# Revit family: Edge_TB42_I_Top_Hung_Standard
name_source: partatom
category: Windows
revit_build: Autodesk Revit 2014 (Build: 20130308_1515(x64)
units: mm (PartAtom-declared; Revit-internal decimal feet)

## types (24) — shared parameters
Aluminium Thickness = 1 mm  [stored 0.00328084 ft]
Bead SG Gap = 13 mm
Bottom Hung = No
Casement Dimension = 42 mm  [stored 0.137795 ft]
Custom Sash Bottom Height = 554 mm  [stored 1.81759 ft]
Custom Sash Top Height = 554 mm  [stored 1.81759 ft]
DG Extrusion Start = 11 mm  [stored 0.0360892 ft]
DG Gasket Finish = Double Glazing Gasket Material
Default Sill Height = 800 mm  [stored 2.62467 ft]
Depth Bead = 28 mm  [stored 0.0918635 ft]
Depth Mullion = 1 mm  [stored 0.00328084 ft]
Description = Thermal break casement windows (42mm), Type I top hung
Frame Center Offset = 21 mm  [stored 0.0688976 ft]
Has Stiffener Cap = Yes
Height Panel 1 = 540 mm  [stored 1.77165 ft]
Height Panel 2 = 540 mm  [stored 1.77165 ft]
Height Sash Bottom = 524 mm  [stored 1.71916 ft]
Height Sash Bottom Opening = 554 mm  [stored 1.81759 ft]
Height Sash Top = 524 mm  [stored 1.71916 ft]
Height Sash Top Opening = 554 mm  [stored 1.81759 ft]
Limit Fixed Pane Height Max = 1800 mm
Limit Fixed Pane Height Min = 200 mm  [stored 0.656168 ft]
Limit Fixed Pane Width Max = 1500 mm
Limit Fixed Pane Width Min = 200 mm  [stored 0.656168 ft]
Limit Sash Bottom Height Min = 300 mm  [stored 0.984252 ft]
Limit Sash Top Height Max = 1200 mm
Limit Sash Top Height Min = 300 mm  [stored 0.984252 ft]
Limit Sash Width Max = 1500 mm
Limit Sash Width Min = 300 mm  [stored 0.984252 ft]
Limit Window Height Max = 1860 mm
Limit Window Height Min = 1400 mm
Manufacturer = Crealco
Max System DG One Piece Thickness = 6 mm  [stored 0.019685 ft]
Max System DG Unit Thickness = 25 mm  [stored 0.082021 ft]
Model = Edge
Mullion Depth Windload Based = 1 mm  [stored 0.00328084 ft]
Offset Bead SG Center Reversed = 21 mm  [stored 0.0688976 ft]
Offset Panel 3 Bead Top = 1170 mm
Offset Sash 1 Top = 23 mm  [stored 0.0754593 ft]
Offset Sash 2 Top = 593 mm  [stored 1.94554 ft]
Offset Sash Left = 23 mm  [stored 0.0754593 ft]
Offset Transom 1 Top = 570 mm  [stored 1.87008 ft]
Offset Transom 2 Top = 1140 mm
Offset Window Exterior = 21 mm  [stored 0.0688976 ft]
SG Gasket Thickness = 6 mm  [stored 0.019685 ft]
Sash Center Offset = 18 mm
Sash Overlap = 7 mm  [stored 0.0229659 ft]
Sash Spacing Inner = 8 mm  [stored 0.0262467 ft]
Top Hung = Yes
URL = http://www.crealco.co.za
Wall Closure = By host
Width Bead = 15 mm  [stored 0.0492126 ft]
Width Profile = 30 mm  [stored 0.0984252 ft]
zero-valued in all types: Window Exterior Offset

## per-type parameters (varying)
- EDGE-1215DT-1000Pa: Area Pane Left Bottom=0.15 m²; Area Pane Left Middle=0.23 m²; Area Pane Left Top=0.23 m²; Area Pane Right=0.78 m²; Clearvue Insulated LowE SHGC Value=0.727; Clearvue Insulated LowE U Value=3.36; Clearvue Insulated SHGC Value=0.8; Clearvue Insulated U Value=4.09; Clearvue SHGC Value=0.888; Clearvue U Value=7.3; Custom Sash Width=554 mm  [stored 1.81759 ft]; Custom Windload=1000 mm  [stored 3.28084 ft]; Custom Window Height=1490 mm; Custom Window Width=1190 mm; DG Thickness Calc=4 mm  [stored 0.0131234 ft]; Energy Advantage SHGC Value=0.794; Energy Advantage U Value=5.3; Height=1490 mm; Height Panel 3=290 mm  [stored 0.951444 ft]; Height Panel 4=1430 mm; Intruderprufe Insulated LowE SHGC Value=0.664; Intruderprufe Insulated LowE U Value=3.31; Intruderprufe Insulated SHGC Value=0.734; Intruderprufe Insulated U Value=4.03; Intruderprufe LowE SHGC Value=0.74; Intruderprufe LowE U Value=5.28; Intruderprufe SHGC Value=0.829; Intruderprufe U Value=7.17; Length Mullion=1490 mm; Length Transom=540 mm  [stored 1.77165 ft]; Limit Sash Bottom Height Max=644 mm  [stored 2.11286 ft]; Limit Sash Bottom Height Max Based On Top Sash=644 mm  [stored 2.11286 ft]; Limit Sash Bottom Height Max Calc=644 mm  [stored 2.11286 ft]; Limit Window Width Max=2130 mm; Limit Window Width Min=830 mm  [stored 2.7231 ft]; Max Pane Area=0.78 m²; Offset Mullion Left=570 mm  [stored 1.87008 ft]; Offset Panel 4 Left=600 mm  [stored 1.9685 ft]; Width=1190 mm; Width Panel 1=540 mm  [stored 1.77165 ft]; Width Panel 2=540 mm  [stored 1.77165 ft]; Width Panel 3=540 mm  [stored 1.77165 ft]; Width Panel 4=560 mm  [stored 1.83727 ft]; Width Sash 1=524 mm  [stored 1.71916 ft]; Width Sash 2=524 mm  [stored 1.71916 ft]; Width Sash Opening=554 mm  [stored 1.81759 ft]; Windload Design=1000 mm  [stored 3.28084 ft]
- EDGE-1515DT-1000Pa: Area Pane Left Bottom=0.15 m²; Area Pane Left Middle=0.23 m²; Area Pane Left Top=0.23 m²; Area Pane Right=1.21 m²; Clearvue Insulated LowE SHGC Value=0.839; Clearvue Insulated LowE U Value=3.59; Clearvue Insulated SHGC Value=0.923; Clearvue Insulated U Value=4.46; Clearvue SHGC Value=1.028; Clearvue U Value=8.22; Custom Sash Width=554 mm  [stored 1.81759 ft]; Custom Windload=1000 mm  [stored 3.28084 ft]; Custom Window Height=1490 mm; Custom Window Width=1490 mm; DG Thickness Calc=4 mm  [stored 0.0131234 ft]; Energy Advantage SHGC Value=0.919; Energy Advantage U Value=5.83; Height=1490 mm; Height Panel 3=290 mm  [stored 0.951444 ft]; Height Panel 4=1430 mm; Intruderprufe Insulated LowE SHGC Value=0.766; Intruderprufe Insulated LowE U Value=3.53; Intruderprufe Insulated SHGC Value=0.848; Intruderprufe Insulated U Value=4.39; Intruderprufe LowE SHGC Value=0.856; Intruderprufe LowE U Value=5.79; Intruderprufe SHGC Value=0.961; Intruderprufe U Value=8.07; Length Mullion=1490 mm; Length Transom=540 mm  [stored 1.77165 ft]; Limit Sash Bottom Height Max=644 mm  [stored 2.11286 ft]; Limit Sash Bottom Height Max Based On Top Sash=644 mm  [stored 2.11286 ft]; Limit Sash Bottom Height Max Calc=644 mm  [stored 2.11286 ft]; Limit Window Width Max=2130 mm; Limit Window Width Min=830 mm  [stored 2.7231 ft]; Max Pane Area=1.21 m²; Offset Mullion Left=570 mm  [stored 1.87008 ft]; Offset Panel 4 Left=600 mm  [stored 1.9685 ft]; Width=1490 mm; Width Panel 1=540 mm  [stored 1.77165 ft]; Width Panel 2=540 mm  [stored 1.77165 ft]; Width Panel 3=540 mm  [stored 1.77165 ft]; Width Panel 4=860 mm  [stored 2.82152 ft]; Width Sash 1=524 mm  [stored 1.71916 ft]; Width Sash 2=524 mm  [stored 1.71916 ft]; Width Sash Opening=554 mm  [stored 1.81759 ft]; Windload Design=1000 mm  [stored 3.28084 ft]
- EDGE-1218DT-1000Pa: Area Pane Left Bottom=0.31 m²; Area Pane Left Middle=0.23 m²; Area Pane Left Top=0.23 m²; Area Pane Right=0.95 m²; Clearvue Insulated LowE SHGC Value=0.789; Clearvue Insulated LowE U Value=3.47; Clearvue Insulated SHGC Value=0.868; Clearvue Insulated U Value=4.26; Clearvue SHGC Value=0.965; Clearvue U Value=7.76; Custom Sash Width=554 mm  [stored 1.81759 ft]; Custom Windload=1000 mm  [stored 3.28084 ft]; Custom Window Height=1790 mm; Custom Window Width=1190 mm; DG Thickness Calc=4 mm  [stored 0.0131234 ft]; Energy Advantage SHGC Value=0.863; Energy Advantage U Value=5.56; Height=1790 mm; Height Panel 3=590 mm; Height Panel 4=1730 mm; Intruderprufe Insulated LowE SHGC Value=0.721; Intruderprufe Insulated LowE U Value=3.41; Intruderprufe Insulated SHGC Value=0.797; Intruderprufe Insulated U Value=4.2; Intruderprufe LowE SHGC Value=0.804; Intruderprufe LowE U Value=5.53; Intruderprufe SHGC Value=0.902; Intruderprufe U Value=7.61; Length Mullion=1790 mm; Length Transom=540 mm  [stored 1.77165 ft]; Limit Sash Bottom Height Max=944 mm; Limit Sash Bottom Height Max Based On Top Sash=944 mm; Limit Sash Bottom Height Max Calc=944 mm; Limit Window Width Max=2130 mm; Limit Window Width Min=830 mm  [stored 2.7231 ft]; Max Pane Area=0.95 m²; Offset Mullion Left=570 mm  [stored 1.87008 ft]; Offset Panel 4 Left=600 mm  [stored 1.9685 ft]; Width=1190 mm; Width Panel 1=540 mm  [stored 1.77165 ft]; Width Panel 2=540 mm  [stored 1.77165 ft]; Width Panel 3=540 mm  [stored 1.77165 ft]; Width Panel 4=560 mm  [stored 1.83727 ft]; Width Sash 1=524 mm  [stored 1.71916 ft]; Width Sash 2=524 mm  [stored 1.71916 ft]; Width Sash Opening=554 mm  [stored 1.81759 ft]; Windload Design=1000 mm  [stored 3.28084 ft]
- EDGE-1518DT-1000Pa: Area Pane Left Bottom=0.31 m²; Area Pane Left Middle=0.23 m²; Area Pane Left Top=0.23 m²; Area Pane Right=1.46 m²; Clearvue Insulated LowE SHGC Value=0.92; Clearvue Insulated LowE U Value=3.77; Clearvue Insulated SHGC Value=1.012; Clearvue Insulated U Value=4.73; Clearvue SHGC Value=0; Clearvue U Value=7.9; Custom Sash Width=554 mm  [stored 1.81759 ft]; Custom Windload=1000 mm  [stored 3.28084 ft]; Custom Window Height=1790 mm; Custom Window Width=1490 mm; DG Thickness Calc=4 mm  [stored 0.0131234 ft]; Energy Advantage SHGC Value=0; Energy Advantage U Value=7.9; Height=1790 mm; Height Panel 3=590 mm; Height Panel 4=1730 mm; Intruderprufe Insulated LowE SHGC Value=0.841; Intruderprufe Insulated LowE U Value=3.7; Intruderprufe Insulated SHGC Value=0.93; Intruderprufe Insulated U Value=4.65; Intruderprufe LowE SHGC Value=0.94; Intruderprufe LowE U Value=6.16; Intruderprufe SHGC Value=1.057; Intruderprufe U Value=8.69; Length Mullion=1790 mm; Length Transom=540 mm  [stored 1.77165 ft]; Limit Sash Bottom Height Max=944 mm; Limit Sash Bottom Height Max Based On Top Sash=944 mm; Limit Sash Bottom Height Max Calc=944 mm; Limit Window Width Max=2130 mm; Limit Window Width Min=830 mm  [stored 2.7231 ft]; Max Pane Area=1.46 m²; Offset Mullion Left=570 mm  [stored 1.87008 ft]; Offset Panel 4 Left=600 mm  [stored 1.9685 ft]; Width=1490 mm; Width Panel 1=540 mm  [stored 1.77165 ft]; Width Panel 2=540 mm  [stored 1.77165 ft]; Width Panel 3=540 mm  [stored 1.77165 ft]; Width Panel 4=860 mm  [stored 2.82152 ft]; Width Sash 1=524 mm  [stored 1.71916 ft]; Width Sash 2=524 mm  [stored 1.71916 ft]; Width Sash Opening=554 mm  [stored 1.81759 ft]; Windload Design=1000 mm  [stored 3.28084 ft]
- EDGE-1815DT-1000Pa: Area Pane Left Bottom=0.23 m²; Area Pane Left Middle=0.38 m²; Area Pane Left Top=0.38 m²; Area Pane Right=1.21 m²; Clearvue Insulated LowE SHGC Value=0.76; Clearvue Insulated LowE U Value=3.32; Clearvue Insulated SHGC Value=0.837; Clearvue Insulated U Value=4.12; Clearvue SHGC Value=0.933; Clearvue U Value=7.56; Custom Sash Width=854 mm  [stored 2.80184 ft]; Custom Windload=1000 mm  [stored 3.28084 ft]; Custom Window Height=1490 mm; Custom Window Width=1790 mm; DG Thickness Calc=4 mm  [stored 0.0131234 ft]; Energy Advantage SHGC Value=0.834; Energy Advantage U Value=5.37; Height=1490 mm; Height Panel 3=290 mm  [stored 0.951444 ft]; Height Panel 4=1430 mm; Intruderprufe Insulated LowE SHGC Value=0.694; Intruderprufe Insulated LowE U Value=3.27; Intruderprufe Insulated SHGC Value=0.769; Intruderprufe Insulated U Value=4.05; Intruderprufe LowE SHGC Value=0.777; Intruderprufe LowE U Value=5.34; Intruderprufe SHGC Value=0.872; Intruderprufe U Value=7.42; Length Mullion=1490 mm; Length Transom=840 mm; Limit Sash Bottom Height Max=644 mm  [stored 2.11286 ft]; Limit Sash Bottom Height Max Based On Top Sash=644 mm  [stored 2.11286 ft]; Limit Sash Bottom Height Max Calc=644 mm  [stored 2.11286 ft]; Limit Window Width Max=2430 mm; Limit Window Width Min=1130 mm; Max Pane Area=1.21 m²; Offset Mullion Left=870 mm; Offset Panel 4 Left=900 mm  [stored 2.95276 ft]; Width=1790 mm; Width Panel 1=840 mm; Width Panel 2=840 mm; Width Panel 3=840 mm; Width Panel 4=860 mm  [stored 2.82152 ft]; Width Sash 1=824 mm; Width Sash 2=824 mm; Width Sash Opening=854 mm  [stored 2.80184 ft]; Windload Design=1000 mm  [stored 3.28084 ft]
- EDGE-2415DT-1000Pa: Area Pane Left Bottom=0.23 m²; Area Pane Left Middle=0.38 m²; Area Pane Left Top=0.38 m²; Area Pane Right=2.06 m²; Clearvue Insulated LowE SHGC Value=0.897; Clearvue Insulated LowE U Value=3.62; Clearvue Insulated SHGC Value=0.988; Clearvue Insulated U Value=4.59; Clearvue SHGC Value=0; Clearvue U Value=7.9; Custom Sash Width=854 mm  [stored 2.80184 ft]; Custom Windload=1000 mm  [stored 3.28084 ft]; Custom Window Height=1490 mm; Custom Window Width=2390 mm; DG Thickness Calc=4 mm  [stored 0.0131234 ft]; Energy Advantage SHGC Value=0; Energy Advantage U Value=7.9; Height=1490 mm; Height Panel 3=290 mm  [stored 0.951444 ft]; Height Panel 4=1430 mm; Intruderprufe Insulated LowE SHGC Value=0.82; Intruderprufe Insulated LowE U Value=3.56; Intruderprufe Insulated SHGC Value=0.908; Intruderprufe Insulated U Value=4.51; Intruderprufe LowE SHGC Value=0.919; Intruderprufe LowE U Value=5.99; Intruderprufe SHGC Value=1.034; Intruderprufe U Value=8.53; Length Mullion=1490 mm; Length Transom=840 mm; Limit Sash Bottom Height Max=644 mm  [stored 2.11286 ft]; Limit Sash Bottom Height Max Based On Top Sash=644 mm  [stored 2.11286 ft]; Limit Sash Bottom Height Max Calc=644 mm  [stored 2.11286 ft]; Limit Window Width Max=2430 mm; Limit Window Width Min=1130 mm; Max Pane Area=2.06 m²; Offset Mullion Left=870 mm; Offset Panel 4 Left=900 mm  [stored 2.95276 ft]; Width=2390 mm; Width Panel 1=840 mm; Width Panel 2=840 mm; Width Panel 3=840 mm; Width Panel 4=1460 mm; Width Sash 1=824 mm; Width Sash 2=824 mm; Width Sash Opening=854 mm  [stored 2.80184 ft]; Windload Design=1000 mm  [stored 3.28084 ft]
- EDGE-1818DT-1000Pa: Area Pane Left Bottom=0.48 m²; Area Pane Left Middle=0.38 m²; Area Pane Left Top=0.38 m²; Area Pane Right=1.46 m²; Clearvue Insulated LowE SHGC Value=0.824; Clearvue Insulated LowE U Value=3.41; Clearvue Insulated SHGC Value=0.907; Clearvue Insulated U Value=4.29; Clearvue SHGC Value=0; Clearvue U Value=7.9; Custom Sash Width=854 mm  [stored 2.80184 ft]; Custom Windload=1000 mm  [stored 3.28084 ft]; Custom Window Height=1790 mm; Custom Window Width=1790 mm; DG Thickness Calc=4 mm  [stored 0.0131234 ft]; Energy Advantage SHGC Value=0; Energy Advantage U Value=7.9; Height=1790 mm; Height Panel 3=590 mm; Height Panel 4=1730 mm; Intruderprufe Insulated LowE SHGC Value=0.753; Intruderprufe Insulated LowE U Value=3.36; Intruderprufe Insulated SHGC Value=0.834; Intruderprufe Insulated U Value=4.22; Intruderprufe LowE SHGC Value=0.843; Intruderprufe LowE U Value=5.58; Intruderprufe SHGC Value=0.948; Intruderprufe U Value=7.87; Length Mullion=1790 mm; Length Transom=840 mm; Limit Sash Bottom Height Max=944 mm; Limit Sash Bottom Height Max Based On Top Sash=944 mm; Limit Sash Bottom Height Max Calc=944 mm; Limit Window Width Max=2430 mm; Limit Window Width Min=1130 mm; Max Pane Area=1.46 m²; Offset Mullion Left=870 mm; Offset Panel 4 Left=900 mm  [stored 2.95276 ft]; Width=1790 mm; Width Panel 1=840 mm; Width Panel 2=840 mm; Width Panel 3=840 mm; Width Panel 4=860 mm  [stored 2.82152 ft]; Width Sash 1=824 mm; Width Sash 2=824 mm; Width Sash Opening=854 mm  [stored 2.80184 ft]; Windload Design=1000 mm  [stored 3.28084 ft]
- EDGE-2418DT-1000Pa: Area Pane Left Bottom=0.48 m²; Area Pane Left Middle=0.38 m²; Area Pane Left Top=0.38 m²; Area Pane Right=2.49 m²; Clearvue Insulated LowE SHGC Value=0; Clearvue Insulated LowE U Value=7.9; Clearvue Insulated SHGC Value=0; Clearvue Insulated U Value=7.9; Clearvue SHGC Value=0; Clearvue U Value=7.9; Custom Sash Width=854 mm  [stored 2.80184 ft]; Custom Windload=1000 mm  [stored 3.28084 ft]; Custom Window Height=1790 mm; Custom Window Width=2390 mm; DG Thickness Calc=5 mm  [stored 0.0164042 ft]; Energy Advantage SHGC Value=0; Energy Advantage U Value=7.9; Height=1790 mm; Height Panel 3=590 mm; Height Panel 4=1730 mm; Intruderprufe Insulated LowE SHGC Value=0.902; Intruderprufe Insulated LowE U Value=3.74; Intruderprufe Insulated SHGC Value=0.999; Intruderprufe Insulated U Value=4.8; Intruderprufe LowE SHGC Value=1.012; Intruderprufe LowE U Value=6.39; Intruderprufe SHGC Value=1.14; Intruderprufe U Value=9.21; Length Mullion=1790 mm; Length Transom=840 mm; Limit Sash Bottom Height Max=944 mm; Limit Sash Bottom Height Max Based On Top Sash=944 mm; Limit Sash Bottom Height Max Calc=944 mm; Limit Window Width Max=2430 mm; Limit Window Width Min=1130 mm; Max Pane Area=2.49 m²; Offset Mullion Left=870 mm; Offset Panel 4 Left=900 mm  [stored 2.95276 ft]; Width=2390 mm; Width Panel 1=840 mm; Width Panel 2=840 mm; Width Panel 3=840 mm; Width Panel 4=1460 mm; Width Sash 1=824 mm; Width Sash 2=824 mm; Width Sash Opening=854 mm  [stored 2.80184 ft]; Windload Design=1000 mm  [stored 3.28084 ft]
- EDGE-1215DT-1500Pa: Area Pane Left Bottom=0.15 m²; Area Pane Left Middle=0.23 m²; Area Pane Left Top=0.23 m²; Area Pane Right=0.78 m²; Clearvue Insulated LowE SHGC Value=0.727; Clearvue Insulated LowE U Value=3.36; Clearvue Insulated SHGC Value=0.8; Clearvue Insulated U Value=4.09; Clearvue SHGC Value=0.888; Clearvue U Value=7.3; Custom Sash Width=554 mm  [stored 1.81759 ft]; Custom Windload=1500 mm; Custom Window Height=1490 mm; Custom Window Width=1190 mm; DG Thickness Calc=4 mm  [stored 0.0131234 ft]; Energy Advantage SHGC Value=0.794; Energy Advantage U Value=5.3; Height=1490 mm; Height Panel 3=290 mm  [stored 0.951444 ft]; Height Panel 4=1430 mm; Intruderprufe Insulated LowE SHGC Value=0.664; Intruderprufe Insulated LowE U Value=3.31; Intruderprufe Insulated SHGC Value=0.734; Intruderprufe Insulated U Value=4.03; Intruderprufe LowE SHGC Value=0.74; Intruderprufe LowE U Value=5.28; Intruderprufe SHGC Value=0.829; Intruderprufe U Value=7.17; Length Mullion=1490 mm; Length Transom=540 mm  [stored 1.77165 ft]; Limit Sash Bottom Height Max=644 mm  [stored 2.11286 ft]; Limit Sash Bottom Height Max Based On Top Sash=644 mm  [stored 2.11286 ft]; Limit Sash Bottom Height Max Calc=644 mm  [stored 2.11286 ft]; Limit Window Width Max=2130 mm; Limit Window Width Min=830 mm  [stored 2.7231 ft]; Max Pane Area=0.78 m²; Offset Mullion Left=570 mm  [stored 1.87008 ft]; Offset Panel 4 Left=600 mm  [stored 1.9685 ft]; Width=1190 mm; Width Panel 1=540 mm  [stored 1.77165 ft]; Width Panel 2=540 mm  [stored 1.77165 ft]; Width Panel 3=540 mm  [stored 1.77165 ft]; Width Panel 4=560 mm  [stored 1.83727 ft]; Width Sash 1=524 mm  [stored 1.71916 ft]; Width Sash 2=524 mm  [stored 1.71916 ft]; Width Sash Opening=554 mm  [stored 1.81759 ft]; Windload Design=1500 mm
- EDGE-1215DT-2000Pa: Area Pane Left Bottom=0.15 m²; Area Pane Left Middle=0.23 m²; Area Pane Left Top=0.23 m²; Area Pane Right=0.78 m²; Clearvue Insulated LowE SHGC Value=0.727; Clearvue Insulated LowE U Value=3.36; Clearvue Insulated SHGC Value=0.8; Clearvue Insulated U Value=4.09; Clearvue SHGC Value=0.888; Clearvue U Value=7.3; Custom Sash Width=554 mm  [stored 1.81759 ft]; Custom Windload=2000 mm; Custom Window Height=1490 mm; Custom Window Width=1190 mm; DG Thickness Calc=4 mm  [stored 0.0131234 ft]; Energy Advantage SHGC Value=0.794; Energy Advantage U Value=5.3; Height=1490 mm; Height Panel 3=290 mm  [stored 0.951444 ft]; Height Panel 4=1430 mm; Intruderprufe Insulated LowE SHGC Value=0.664; Intruderprufe Insulated LowE U Value=3.31; Intruderprufe Insulated SHGC Value=0.734; Intruderprufe Insulated U Value=4.03; Intruderprufe LowE SHGC Value=0.74; Intruderprufe LowE U Value=5.28; Intruderprufe SHGC Value=0.829; Intruderprufe U Value=7.17; Length Mullion=1490 mm; Length Transom=540 mm  [stored 1.77165 ft]; Limit Sash Bottom Height Max=644 mm  [stored 2.11286 ft]; Limit Sash Bottom Height Max Based On Top Sash=644 mm  [stored 2.11286 ft]; Limit Sash Bottom Height Max Calc=644 mm  [stored 2.11286 ft]; Limit Window Width Max=2130 mm; Limit Window Width Min=830 mm  [stored 2.7231 ft]; Max Pane Area=0.78 m²; Offset Mullion Left=570 mm  [stored 1.87008 ft]; Offset Panel 4 Left=600 mm  [stored 1.9685 ft]; Width=1190 mm; Width Panel 1=540 mm  [stored 1.77165 ft]; Width Panel 2=540 mm  [stored 1.77165 ft]; Width Panel 3=540 mm  [stored 1.77165 ft]; Width Panel 4=560 mm  [stored 1.83727 ft]; Width Sash 1=524 mm  [stored 1.71916 ft]; Width Sash 2=524 mm  [stored 1.71916 ft]; Width Sash Opening=554 mm  [stored 1.81759 ft]; Windload Design=2000 mm
- EDGE-1515DT-1500Pa: Area Pane Left Bottom=0.15 m²; Area Pane Left Middle=0.23 m²; Area Pane Left Top=0.23 m²; Area Pane Right=1.21 m²; Clearvue Insulated LowE SHGC Value=0.839; Clearvue Insulated LowE U Value=3.59; Clearvue Insulated SHGC Value=0.923; Clearvue Insulated U Value=4.46; Clearvue SHGC Value=1.028; Clearvue U Value=8.22; Custom Sash Width=554 mm  [stored 1.81759 ft]; Custom Windload=1500 mm; Custom Window Height=1490 mm; Custom Window Width=1490 mm; DG Thickness Calc=4 mm  [stored 0.0131234 ft]; Energy Advantage SHGC Value=0.919; Energy Advantage U Value=5.83; Height=1490 mm; Height Panel 3=290 mm  [stored 0.951444 ft]; Height Panel 4=1430 mm; Intruderprufe Insulated LowE SHGC Value=0.766; Intruderprufe Insulated LowE U Value=3.53; Intruderprufe Insulated SHGC Value=0.848; Intruderprufe Insulated U Value=4.39; Intruderprufe LowE SHGC Value=0.856; Intruderprufe LowE U Value=5.79; Intruderprufe SHGC Value=0.961; Intruderprufe U Value=8.07; Length Mullion=1490 mm; Length Transom=540 mm  [stored 1.77165 ft]; Limit Sash Bottom Height Max=644 mm  [stored 2.11286 ft]; Limit Sash Bottom Height Max Based On Top Sash=644 mm  [stored 2.11286 ft]; Limit Sash Bottom Height Max Calc=644 mm  [stored 2.11286 ft]; Limit Window Width Max=2130 mm; Limit Window Width Min=830 mm  [stored 2.7231 ft]; Max Pane Area=1.21 m²; Offset Mullion Left=570 mm  [stored 1.87008 ft]; Offset Panel 4 Left=600 mm  [stored 1.9685 ft]; Width=1490 mm; Width Panel 1=540 mm  [stored 1.77165 ft]; Width Panel 2=540 mm  [stored 1.77165 ft]; Width Panel 3=540 mm  [stored 1.77165 ft]; Width Panel 4=860 mm  [stored 2.82152 ft]; Width Sash 1=524 mm  [stored 1.71916 ft]; Width Sash 2=524 mm  [stored 1.71916 ft]; Width Sash Opening=554 mm  [stored 1.81759 ft]; Windload Design=1500 mm
- EDGE-1515DT-2000Pa: Area Pane Left Bottom=0.15 m²; Area Pane Left Middle=0.23 m²; Area Pane Left Top=0.23 m²; Area Pane Right=1.21 m²; Clearvue Insulated LowE SHGC Value=0.839; Clearvue Insulated LowE U Value=3.59; Clearvue Insulated SHGC Value=0.923; Clearvue Insulated U Value=4.46; Clearvue SHGC Value=1.028; Clearvue U Value=8.22; Custom Sash Width=554 mm  [stored 1.81759 ft]; Custom Windload=2000 mm; Custom Window Height=1490 mm; Custom Window Width=1490 mm; DG Thickness Calc=4 mm  [stored 0.0131234 ft]; Energy Advantage SHGC Value=0.919; Energy Advantage U Value=5.83; Height=1490 mm; Height Panel 3=290 mm  [stored 0.951444 ft]; Height Panel 4=1430 mm; Intruderprufe Insulated LowE SHGC Value=0.766; Intruderprufe Insulated LowE U Value=3.53; Intruderprufe Insulated SHGC Value=0.848; Intruderprufe Insulated U Value=4.39; Intruderprufe LowE SHGC Value=0.856; Intruderprufe LowE U Value=5.79; Intruderprufe SHGC Value=0.961; Intruderprufe U Value=8.07; Length Mullion=1490 mm; Length Transom=540 mm  [stored 1.77165 ft]; Limit Sash Bottom Height Max=644 mm  [stored 2.11286 ft]; Limit Sash Bottom Height Max Based On Top Sash=644 mm  [stored 2.11286 ft]; Limit Sash Bottom Height Max Calc=644 mm  [stored 2.11286 ft]; Limit Window Width Max=2130 mm; Limit Window Width Min=830 mm  [stored 2.7231 ft]; Max Pane Area=1.21 m²; Offset Mullion Left=570 mm  [stored 1.87008 ft]; Offset Panel 4 Left=600 mm  [stored 1.9685 ft]; Width=1490 mm; Width Panel 1=540 mm  [stored 1.77165 ft]; Width Panel 2=540 mm  [stored 1.77165 ft]; Width Panel 3=540 mm  [stored 1.77165 ft]; Width Panel 4=860 mm  [stored 2.82152 ft]; Width Sash 1=524 mm  [stored 1.71916 ft]; Width Sash 2=524 mm  [stored 1.71916 ft]; Width Sash Opening=554 mm  [stored 1.81759 ft]; Windload Design=2000 mm
- EDGE-1815DT-1500Pa: Area Pane Left Bottom=0.23 m²; Area Pane Left Middle=0.38 m²; Area Pane Left Top=0.38 m²; Area Pane Right=1.21 m²; Clearvue Insulated LowE SHGC Value=0.76; Clearvue Insulated LowE U Value=3.32; Clearvue Insulated SHGC Value=0.837; Clearvue Insulated U Value=4.12; Clearvue SHGC Value=0.933; Clearvue U Value=7.56; Custom Sash Width=854 mm  [stored 2.80184 ft]; Custom Windload=1500 mm; Custom Window Height=1490 mm; Custom Window Width=1790 mm; DG Thickness Calc=4 mm  [stored 0.0131234 ft]; Energy Advantage SHGC Value=0.834; Energy Advantage U Value=5.37; Height=1490 mm; Height Panel 3=290 mm  [stored 0.951444 ft]; Height Panel 4=1430 mm; Intruderprufe Insulated LowE SHGC Value=0.694; Intruderprufe Insulated LowE U Value=3.27; Intruderprufe Insulated SHGC Value=0.769; Intruderprufe Insulated U Value=4.05; Intruderprufe LowE SHGC Value=0.777; Intruderprufe LowE U Value=5.34; Intruderprufe SHGC Value=0.872; Intruderprufe U Value=7.42; Length Mullion=1490 mm; Length Transom=840 mm; Limit Sash Bottom Height Max=644 mm  [stored 2.11286 ft]; Limit Sash Bottom Height Max Based On Top Sash=644 mm  [stored 2.11286 ft]; Limit Sash Bottom Height Max Calc=644 mm  [stored 2.11286 ft]; Limit Window Width Max=2430 mm; Limit Window Width Min=1130 mm; Max Pane Area=1.21 m²; Offset Mullion Left=870 mm; Offset Panel 4 Left=900 mm  [stored 2.95276 ft]; Width=1790 mm; Width Panel 1=840 mm; Width Panel 2=840 mm; Width Panel 3=840 mm; Width Panel 4=860 mm  [stored 2.82152 ft]; Width Sash 1=824 mm; Width Sash 2=824 mm; Width Sash Opening=854 mm  [stored 2.80184 ft]; Windload Design=1500 mm
- EDGE-1815DT-2000Pa: Area Pane Left Bottom=0.23 m²; Area Pane Left Middle=0.38 m²; Area Pane Left Top=0.38 m²; Area Pane Right=1.21 m²; Clearvue Insulated LowE SHGC Value=0.76; Clearvue Insulated LowE U Value=3.32; Clearvue Insulated SHGC Value=0.837; Clearvue Insulated U Value=4.12; Clearvue SHGC Value=0.933; Clearvue U Value=7.56; Custom Sash Width=854 mm  [stored 2.80184 ft]; Custom Windload=2000 mm; Custom Window Height=1490 mm; Custom Window Width=1790 mm; DG Thickness Calc=4 mm  [stored 0.0131234 ft]; Energy Advantage SHGC Value=0.834; Energy Advantage U Value=5.37; Height=1490 mm; Height Panel 3=290 mm  [stored 0.951444 ft]; Height Panel 4=1430 mm; Intruderprufe Insulated LowE SHGC Value=0.694; Intruderprufe Insulated LowE U Value=3.27; Intruderprufe Insulated SHGC Value=0.769; Intruderprufe Insulated U Value=4.05; Intruderprufe LowE SHGC Value=0.777; Intruderprufe LowE U Value=5.34; Intruderprufe SHGC Value=0.872; Intruderprufe U Value=7.42; Length Mullion=1490 mm; Length Transom=840 mm; Limit Sash Bottom Height Max=644 mm  [stored 2.11286 ft]; Limit Sash Bottom Height Max Based On Top Sash=644 mm  [stored 2.11286 ft]; Limit Sash Bottom Height Max Calc=644 mm  [stored 2.11286 ft]; Limit Window Width Max=2430 mm; Limit Window Width Min=1130 mm; Max Pane Area=1.21 m²; Offset Mullion Left=870 mm; Offset Panel 4 Left=900 mm  [stored 2.95276 ft]; Width=1790 mm; Width Panel 1=840 mm; Width Panel 2=840 mm; Width Panel 3=840 mm; Width Panel 4=860 mm  [stored 2.82152 ft]; Width Sash 1=824 mm; Width Sash 2=824 mm; Width Sash Opening=854 mm  [stored 2.80184 ft]; Windload Design=2000 mm
- EDGE-2415DT-1500Pa: Area Pane Left Bottom=0.23 m²; Area Pane Left Middle=0.38 m²; Area Pane Left Top=0.38 m²; Area Pane Right=2.06 m²; Clearvue Insulated LowE SHGC Value=0.897; Clearvue Insulated LowE U Value=3.62; Clearvue Insulated SHGC Value=0.988; Clearvue Insulated U Value=4.59; Clearvue SHGC Value=0; Clearvue U Value=7.9; Custom Sash Width=854 mm  [stored 2.80184 ft]; Custom Windload=1500 mm; Custom Window Height=1490 mm; Custom Window Width=2390 mm; DG Thickness Calc=4 mm  [stored 0.0131234 ft]; Energy Advantage SHGC Value=0; Energy Advantage U Value=7.9; Height=1490 mm; Height Panel 3=290 mm  [stored 0.951444 ft]; Height Panel 4=1430 mm; Intruderprufe Insulated LowE SHGC Value=0.82; Intruderprufe Insulated LowE U Value=3.56; Intruderprufe Insulated SHGC Value=0.908; Intruderprufe Insulated U Value=4.51; Intruderprufe LowE SHGC Value=0.919; Intruderprufe LowE U Value=5.99; Intruderprufe SHGC Value=1.034; Intruderprufe U Value=8.53; Length Mullion=1490 mm; Length Transom=840 mm; Limit Sash Bottom Height Max=644 mm  [stored 2.11286 ft]; Limit Sash Bottom Height Max Based On Top Sash=644 mm  [stored 2.11286 ft]; Limit Sash Bottom Height Max Calc=644 mm  [stored 2.11286 ft]; Limit Window Width Max=2430 mm; Limit Window Width Min=1130 mm; Max Pane Area=2.06 m²; Offset Mullion Left=870 mm; Offset Panel 4 Left=900 mm  [stored 2.95276 ft]; Width=2390 mm; Width Panel 1=840 mm; Width Panel 2=840 mm; Width Panel 3=840 mm; Width Panel 4=1460 mm; Width Sash 1=824 mm; Width Sash 2=824 mm; Width Sash Opening=854 mm  [stored 2.80184 ft]; Windload Design=1500 mm
- EDGE-2415DT-2000Pa: Area Pane Left Bottom=0.23 m²; Area Pane Left Middle=0.38 m²; Area Pane Left Top=0.38 m²; Area Pane Right=2.06 m²; Clearvue Insulated LowE SHGC Value=0.897; Clearvue Insulated LowE U Value=3.62; Clearvue Insulated SHGC Value=0.988; Clearvue Insulated U Value=4.59; Clearvue SHGC Value=0; Clearvue U Value=7.9; Custom Sash Width=854 mm  [stored 2.80184 ft]; Custom Windload=2000 mm; Custom Window Height=1490 mm; Custom Window Width=2390 mm; DG Thickness Calc=4 mm  [stored 0.0131234 ft]; Energy Advantage SHGC Value=0; Energy Advantage U Value=7.9; Height=1490 mm; Height Panel 3=290 mm  [stored 0.951444 ft]; Height Panel 4=1430 mm; Intruderprufe Insulated LowE SHGC Value=0.82; Intruderprufe Insulated LowE U Value=3.56; Intruderprufe Insulated SHGC Value=0.908; Intruderprufe Insulated U Value=4.51; Intruderprufe LowE SHGC Value=0.919; Intruderprufe LowE U Value=5.99; Intruderprufe SHGC Value=1.034; Intruderprufe U Value=8.53; Length Mullion=1490 mm; Length Transom=840 mm; Limit Sash Bottom Height Max=644 mm  [stored 2.11286 ft]; Limit Sash Bottom Height Max Based On Top Sash=644 mm  [stored 2.11286 ft]; Limit Sash Bottom Height Max Calc=644 mm  [stored 2.11286 ft]; Limit Window Width Max=2430 mm; Limit Window Width Min=1130 mm; Max Pane Area=2.06 m²; Offset Mullion Left=870 mm; Offset Panel 4 Left=900 mm  [stored 2.95276 ft]; Width=2390 mm; Width Panel 1=840 mm; Width Panel 2=840 mm; Width Panel 3=840 mm; Width Panel 4=1460 mm; Width Sash 1=824 mm; Width Sash 2=824 mm; Width Sash Opening=854 mm  [stored 2.80184 ft]; Windload Design=2000 mm
- EDGE-1218DT-1500Pa: Area Pane Left Bottom=0.31 m²; Area Pane Left Middle=0.23 m²; Area Pane Left Top=0.23 m²; Area Pane Right=0.95 m²; Clearvue Insulated LowE SHGC Value=0.789; Clearvue Insulated LowE U Value=3.47; Clearvue Insulated SHGC Value=0.868; Clearvue Insulated U Value=4.26; Clearvue SHGC Value=0.965; Clearvue U Value=7.76; Custom Sash Width=554 mm  [stored 1.81759 ft]; Custom Windload=1500 mm; Custom Window Height=1790 mm; Custom Window Width=1190 mm; DG Thickness Calc=4 mm  [stored 0.0131234 ft]; Energy Advantage SHGC Value=0.863; Energy Advantage U Value=5.56; Height=1790 mm; Height Panel 3=590 mm; Height Panel 4=1730 mm; Intruderprufe Insulated LowE SHGC Value=0.721; Intruderprufe Insulated LowE U Value=3.41; Intruderprufe Insulated SHGC Value=0.797; Intruderprufe Insulated U Value=4.2; Intruderprufe LowE SHGC Value=0.804; Intruderprufe LowE U Value=5.53; Intruderprufe SHGC Value=0.902; Intruderprufe U Value=7.61; Length Mullion=1790 mm; Length Transom=540 mm  [stored 1.77165 ft]; Limit Sash Bottom Height Max=944 mm; Limit Sash Bottom Height Max Based On Top Sash=944 mm; Limit Sash Bottom Height Max Calc=944 mm; Limit Window Width Max=2130 mm; Limit Window Width Min=830 mm  [stored 2.7231 ft]; Max Pane Area=0.95 m²; Offset Mullion Left=570 mm  [stored 1.87008 ft]; Offset Panel 4 Left=600 mm  [stored 1.9685 ft]; Width=1190 mm; Width Panel 1=540 mm  [stored 1.77165 ft]; Width Panel 2=540 mm  [stored 1.77165 ft]; Width Panel 3=540 mm  [stored 1.77165 ft]; Width Panel 4=560 mm  [stored 1.83727 ft]; Width Sash 1=524 mm  [stored 1.71916 ft]; Width Sash 2=524 mm  [stored 1.71916 ft]; Width Sash Opening=554 mm  [stored 1.81759 ft]; Windload Design=1500 mm
- EDGE-1218DT-2000Pa: Area Pane Left Bottom=0.31 m²; Area Pane Left Middle=0.23 m²; Area Pane Left Top=0.23 m²; Area Pane Right=0.95 m²; Clearvue Insulated LowE SHGC Value=0.789; Clearvue Insulated LowE U Value=3.47; Clearvue Insulated SHGC Value=0.868; Clearvue Insulated U Value=4.26; Clearvue SHGC Value=0.965; Clearvue U Value=7.76; Custom Sash Width=554 mm  [stored 1.81759 ft]; Custom Windload=2000 mm; Custom Window Height=1790 mm; Custom Window Width=1190 mm; DG Thickness Calc=4 mm  [stored 0.0131234 ft]; Energy Advantage SHGC Value=0.863; Energy Advantage U Value=5.56; Height=1790 mm; Height Panel 3=590 mm; Height Panel 4=1730 mm; Intruderprufe Insulated LowE SHGC Value=0.721; Intruderprufe Insulated LowE U Value=3.41; Intruderprufe Insulated SHGC Value=0.797; Intruderprufe Insulated U Value=4.2; Intruderprufe LowE SHGC Value=0.804; Intruderprufe LowE U Value=5.53; Intruderprufe SHGC Value=0.902; Intruderprufe U Value=7.61; Length Mullion=1790 mm; Length Transom=540 mm  [stored 1.77165 ft]; Limit Sash Bottom Height Max=944 mm; Limit Sash Bottom Height Max Based On Top Sash=944 mm; Limit Sash Bottom Height Max Calc=944 mm; Limit Window Width Max=2130 mm; Limit Window Width Min=830 mm  [stored 2.7231 ft]; Max Pane Area=0.95 m²; Offset Mullion Left=570 mm  [stored 1.87008 ft]; Offset Panel 4 Left=600 mm  [stored 1.9685 ft]; Width=1190 mm; Width Panel 1=540 mm  [stored 1.77165 ft]; Width Panel 2=540 mm  [stored 1.77165 ft]; Width Panel 3=540 mm  [stored 1.77165 ft]; Width Panel 4=560 mm  [stored 1.83727 ft]; Width Sash 1=524 mm  [stored 1.71916 ft]; Width Sash 2=524 mm  [stored 1.71916 ft]; Width Sash Opening=554 mm  [stored 1.81759 ft]; Windload Design=2000 mm
- EDGE-1518DT-1500Pa: Area Pane Left Bottom=0.31 m²; Area Pane Left Middle=0.23 m²; Area Pane Left Top=0.23 m²; Area Pane Right=1.46 m²; Clearvue Insulated LowE SHGC Value=0.92; Clearvue Insulated LowE U Value=3.77; Clearvue Insulated SHGC Value=1.012; Clearvue Insulated U Value=4.73; Clearvue SHGC Value=0; Clearvue U Value=7.9; Custom Sash Width=554 mm  [stored 1.81759 ft]; Custom Windload=1500 mm; Custom Window Height=1790 mm; Custom Window Width=1490 mm; DG Thickness Calc=4 mm  [stored 0.0131234 ft]; Energy Advantage SHGC Value=0; Energy Advantage U Value=7.9; Height=1790 mm; Height Panel 3=590 mm; Height Panel 4=1730 mm; Intruderprufe Insulated LowE SHGC Value=0.841; Intruderprufe Insulated LowE U Value=3.7; Intruderprufe Insulated SHGC Value=0.93; Intruderprufe Insulated U Value=4.65; Intruderprufe LowE SHGC Value=0.94; Intruderprufe LowE U Value=6.16; Intruderprufe SHGC Value=1.057; Intruderprufe U Value=8.69; Length Mullion=1790 mm; Length Transom=540 mm  [stored 1.77165 ft]; Limit Sash Bottom Height Max=944 mm; Limit Sash Bottom Height Max Based On Top Sash=944 mm; Limit Sash Bottom Height Max Calc=944 mm; Limit Window Width Max=2130 mm; Limit Window Width Min=830 mm  [stored 2.7231 ft]; Max Pane Area=1.46 m²; Offset Mullion Left=570 mm  [stored 1.87008 ft]; Offset Panel 4 Left=600 mm  [stored 1.9685 ft]; Width=1490 mm; Width Panel 1=540 mm  [stored 1.77165 ft]; Width Panel 2=540 mm  [stored 1.77165 ft]; Width Panel 3=540 mm  [stored 1.77165 ft]; Width Panel 4=860 mm  [stored 2.82152 ft]; Width Sash 1=524 mm  [stored 1.71916 ft]; Width Sash 2=524 mm  [stored 1.71916 ft]; Width Sash Opening=554 mm  [stored 1.81759 ft]; Windload Design=1500 mm
- EDGE-1518DT-2000Pa: Area Pane Left Bottom=0.31 m²; Area Pane Left Middle=0.23 m²; Area Pane Left Top=0.23 m²; Area Pane Right=1.46 m²; Clearvue Insulated LowE SHGC Value=0.92; Clearvue Insulated LowE U Value=3.77; Clearvue Insulated SHGC Value=1.012; Clearvue Insulated U Value=4.73; Clearvue SHGC Value=0; Clearvue U Value=7.9; Custom Sash Width=554 mm  [stored 1.81759 ft]; Custom Windload=2000 mm; Custom Window Height=1790 mm; Custom Window Width=1490 mm; DG Thickness Calc=4 mm  [stored 0.0131234 ft]; Energy Advantage SHGC Value=0; Energy Advantage U Value=7.9; Height=1790 mm; Height Panel 3=590 mm; Height Panel 4=1730 mm; Intruderprufe Insulated LowE SHGC Value=0.841; Intruderprufe Insulated LowE U Value=3.7; Intruderprufe Insulated SHGC Value=0.93; Intruderprufe Insulated U Value=4.65; Intruderprufe LowE SHGC Value=0.94; Intruderprufe LowE U Value=6.16; Intruderprufe SHGC Value=1.057; Intruderprufe U Value=8.69; Length Mullion=1790 mm; Length Transom=540 mm  [stored 1.77165 ft]; Limit Sash Bottom Height Max=944 mm; Limit Sash Bottom Height Max Based On Top Sash=944 mm; Limit Sash Bottom Height Max Calc=944 mm; Limit Window Width Max=2130 mm; Limit Window Width Min=830 mm  [stored 2.7231 ft]; Max Pane Area=1.46 m²; Offset Mullion Left=570 mm  [stored 1.87008 ft]; Offset Panel 4 Left=600 mm  [stored 1.9685 ft]; Width=1490 mm; Width Panel 1=540 mm  [stored 1.77165 ft]; Width Panel 2=540 mm  [stored 1.77165 ft]; Width Panel 3=540 mm  [stored 1.77165 ft]; Width Panel 4=860 mm  [stored 2.82152 ft]; Width Sash 1=524 mm  [stored 1.71916 ft]; Width Sash 2=524 mm  [stored 1.71916 ft]; Width Sash Opening=554 mm  [stored 1.81759 ft]; Windload Design=2000 mm
- EDGE-1818DT-1500Pa: Area Pane Left Bottom=0.48 m²; Area Pane Left Middle=0.38 m²; Area Pane Left Top=0.38 m²; Area Pane Right=1.46 m²; Clearvue Insulated LowE SHGC Value=0.824; Clearvue Insulated LowE U Value=3.41; Clearvue Insulated SHGC Value=0.907; Clearvue Insulated U Value=4.29; Clearvue SHGC Value=0; Clearvue U Value=7.9; Custom Sash Width=854 mm  [stored 2.80184 ft]; Custom Windload=1500 mm; Custom Window Height=1790 mm; Custom Window Width=1790 mm; DG Thickness Calc=4 mm  [stored 0.0131234 ft]; Energy Advantage SHGC Value=0; Energy Advantage U Value=7.9; Height=1790 mm; Height Panel 3=590 mm; Height Panel 4=1730 mm; Intruderprufe Insulated LowE SHGC Value=0.753; Intruderprufe Insulated LowE U Value=3.36; Intruderprufe Insulated SHGC Value=0.834; Intruderprufe Insulated U Value=4.22; Intruderprufe LowE SHGC Value=0.843; Intruderprufe LowE U Value=5.58; Intruderprufe SHGC Value=0.948; Intruderprufe U Value=7.87; Length Mullion=1790 mm; Length Transom=840 mm; Limit Sash Bottom Height Max=944 mm; Limit Sash Bottom Height Max Based On Top Sash=944 mm; Limit Sash Bottom Height Max Calc=944 mm; Limit Window Width Max=2430 mm; Limit Window Width Min=1130 mm; Max Pane Area=1.46 m²; Offset Mullion Left=870 mm; Offset Panel 4 Left=900 mm  [stored 2.95276 ft]; Width=1790 mm; Width Panel 1=840 mm; Width Panel 2=840 mm; Width Panel 3=840 mm; Width Panel 4=860 mm  [stored 2.82152 ft]; Width Sash 1=824 mm; Width Sash 2=824 mm; Width Sash Opening=854 mm  [stored 2.80184 ft]; Windload Design=1500 mm
- EDGE-1818DT-2000Pa: Area Pane Left Bottom=0.48 m²; Area Pane Left Middle=0.38 m²; Area Pane Left Top=0.38 m²; Area Pane Right=1.46 m²; Clearvue Insulated LowE SHGC Value=0.824; Clearvue Insulated LowE U Value=3.41; Clearvue Insulated SHGC Value=0.907; Clearvue Insulated U Value=4.29; Clearvue SHGC Value=0; Clearvue U Value=7.9; Custom Sash Width=854 mm  [stored 2.80184 ft]; Custom Windload=2000 mm; Custom Window Height=1790 mm; Custom Window Width=1790 mm; DG Thickness Calc=4 mm  [stored 0.0131234 ft]; Energy Advantage SHGC Value=0; Energy Advantage U Value=7.9; Height=1790 mm; Height Panel 3=590 mm; Height Panel 4=1730 mm; Intruderprufe Insulated LowE SHGC Value=0.753; Intruderprufe Insulated LowE U Value=3.36; Intruderprufe Insulated SHGC Value=0.834; Intruderprufe Insulated U Value=4.22; Intruderprufe LowE SHGC Value=0.843; Intruderprufe LowE U Value=5.58; Intruderprufe SHGC Value=0.948; Intruderprufe U Value=7.87; Length Mullion=1790 mm; Length Transom=840 mm; Limit Sash Bottom Height Max=944 mm; Limit Sash Bottom Height Max Based On Top Sash=944 mm; Limit Sash Bottom Height Max Calc=944 mm; Limit Window Width Max=2430 mm; Limit Window Width Min=1130 mm; Max Pane Area=1.46 m²; Offset Mullion Left=870 mm; Offset Panel 4 Left=900 mm  [stored 2.95276 ft]; Width=1790 mm; Width Panel 1=840 mm; Width Panel 2=840 mm; Width Panel 3=840 mm; Width Panel 4=860 mm  [stored 2.82152 ft]; Width Sash 1=824 mm; Width Sash 2=824 mm; Width Sash Opening=854 mm  [stored 2.80184 ft]; Windload Design=2000 mm
- EDGE-2418DT-1500Pa: Area Pane Left Bottom=0.48 m²; Area Pane Left Middle=0.38 m²; Area Pane Left Top=0.38 m²; Area Pane Right=2.49 m²; Clearvue Insulated LowE SHGC Value=0; Clearvue Insulated LowE U Value=7.9; Clearvue Insulated SHGC Value=0; Clearvue Insulated U Value=7.9; Clearvue SHGC Value=0; Clearvue U Value=7.9; Custom Sash Width=854 mm  [stored 2.80184 ft]; Custom Windload=1500 mm; Custom Window Height=1790 mm; Custom Window Width=2390 mm; DG Thickness Calc=5 mm  [stored 0.0164042 ft]; Energy Advantage SHGC Value=0; Energy Advantage U Value=7.9; Height=1790 mm; Height Panel 3=590 mm; Height Panel 4=1730 mm; Intruderprufe Insulated LowE SHGC Value=0.902; Intruderprufe Insulated LowE U Value=3.74; Intruderprufe Insulated SHGC Value=0.999; Intruderprufe Insulated U Value=4.8; Intruderprufe LowE SHGC Value=1.012; Intruderprufe LowE U Value=6.39; Intruderprufe SHGC Value=1.14; Intruderprufe U Value=9.21; Length Mullion=1790 mm; Length Transom=840 mm; Limit Sash Bottom Height Max=944 mm; Limit Sash Bottom Height Max Based On Top Sash=944 mm; Limit Sash Bottom Height Max Calc=944 mm; Limit Window Width Max=2430 mm; Limit Window Width Min=1130 mm; Max Pane Area=2.49 m²; Offset Mullion Left=870 mm; Offset Panel 4 Left=900 mm  [stored 2.95276 ft]; Width=2390 mm; Width Panel 1=840 mm; Width Panel 2=840 mm; Width Panel 3=840 mm; Width Panel 4=1460 mm; Width Sash 1=824 mm; Width Sash 2=824 mm; Width Sash Opening=854 mm  [stored 2.80184 ft]; Windload Design=1500 mm
- EDGE-2418DT-2000Pa: Area Pane Left Bottom=0.48 m²; Area Pane Left Middle=0.38 m²; Area Pane Left Top=0.38 m²; Area Pane Right=2.49 m²; Clearvue Insulated LowE SHGC Value=0; Clearvue Insulated LowE U Value=7.9; Clearvue Insulated SHGC Value=0; Clearvue Insulated U Value=7.9; Clearvue SHGC Value=0; Clearvue U Value=7.9; Custom Sash Width=854 mm  [stored 2.80184 ft]; Custom Windload=2000 mm; Custom Window Height=1790 mm; Custom Window Width=2390 mm; DG Thickness Calc=5 mm  [stored 0.0164042 ft]; Energy Advantage SHGC Value=0; Energy Advantage U Value=7.9; Height=1790 mm; Height Panel 3=590 mm; Height Panel 4=1730 mm; Intruderprufe Insulated LowE SHGC Value=0.902; Intruderprufe Insulated LowE U Value=3.74; Intruderprufe Insulated SHGC Value=0.999; Intruderprufe Insulated U Value=4.8; Intruderprufe LowE SHGC Value=1.012; Intruderprufe LowE U Value=6.39; Intruderprufe SHGC Value=1.14; Intruderprufe U Value=9.21; Length Mullion=1790 mm; Length Transom=840 mm; Limit Sash Bottom Height Max=944 mm; Limit Sash Bottom Height Max Based On Top Sash=944 mm; Limit Sash Bottom Height Max Calc=944 mm; Limit Window Width Max=2430 mm; Limit Window Width Min=1130 mm; Max Pane Area=2.49 m²; Offset Mullion Left=870 mm; Offset Panel 4 Left=900 mm  [stored 2.95276 ft]; Width=2390 mm; Width Panel 1=840 mm; Width Panel 2=840 mm; Width Panel 3=840 mm; Width Panel 4=1460 mm; Width Sash 1=824 mm; Width Sash 2=824 mm; Width Sash Opening=854 mm  [stored 2.80184 ft]; Windload Design=2000 mm

note: [stored X ft] marks values corroborated as IEEE doubles in the binary element streams (Revit-internal decimal feet)

## geometry (parser evidence)
native form markers: Blend x4, Extrusion x1, Sweep x33
no freeform markers — native parametric forms only
